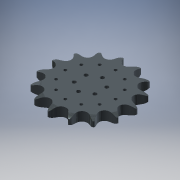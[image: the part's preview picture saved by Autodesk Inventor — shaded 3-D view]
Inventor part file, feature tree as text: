
AUTODESK INVENTOR PART (.ipt)
format: ipt  version: 2016 (Build 200138000, 138)  size: 622,080 bytes
history: native  units: mm
features: other x7, extrude x5, sketch x3, pattern_linear x1, pattern_circular x1
ambient origin geometry x8: Origin, YZ Plane, XZ Plane, XY Plane, X Axis, Y Axis, Z Axis, Center Point
bodies: Solid1 (feature_tree)
feature tree (17):
  other  "drive_sprocket_inner"
  other  "Theoretical Tooth Profile"
  other  "Tooth Profile"
  other  "Section Profile"
  other  "Shroud"
  other  "Strand"
  pattern_linear  "Strand Pattern"  Spacing1=22.514747mm  [1 undecoded]
  extrude  "Theoretical Tooth"  Depth=2.5mm
  extrude  "Tooth"  Depth=2.5mm
  pattern_circular  "Tooth Pattern"  [2 undecoded]
  other  "Timing Plane"
  extrude  "Extrusion4"  Depth=2.5mm
  extrude  "Extrusion5"  Depth=10.0mm TaperAngle=0.0deg
  extrude  "Extrusion6"  Depth=2.5mm
  sketch  "Sketch4"  dims[d0=61.083626mm]
  sketch  "Sketch5"  dims[d2=4.18879mm]
  sketch  "Sketch6"  dims[d3=4.29755mm d10=22.514747mm d11=2.490003mm d12=6.808mm d13=11.10555mm d14=11.914mm d18=10.0mm d19=0.0mm d20=150.0mm d21=360.0deg d23=3.81mm d28=0.0mm d29=0.0mm d30=7.2075mm d31=38.850402mm d32=7.2075mm d33=1.5875mm d34=12.7mm d36=90.0deg d37=90.0deg d38=10.0mm d40=13.92mm d42=0.0mm d43=3.60375mm d44=23.387412mm d45=17.3604mm d46=4.29755mm d47=10.0mm d48=0.0mm d49=0.0mm d50=10.0mm d51=9.5mm d52=3.0mm d53=60.0mm d55=360.0deg d57=0.0mm d58=0.0mm d59=20.0mm d60=2.35mm d61=120.0mm d63=360.0deg d65=0.0mm d66=0.0mm d67=7.0mm d68=60.0mm d70=360.0deg d72=2.5mm d73=0.0mm]
note: 3 required parameter values undecoded (feature->parameter linkage not recoverable at this tier; creation-order binding heuristic only, values carry confidence <= 0.55)
